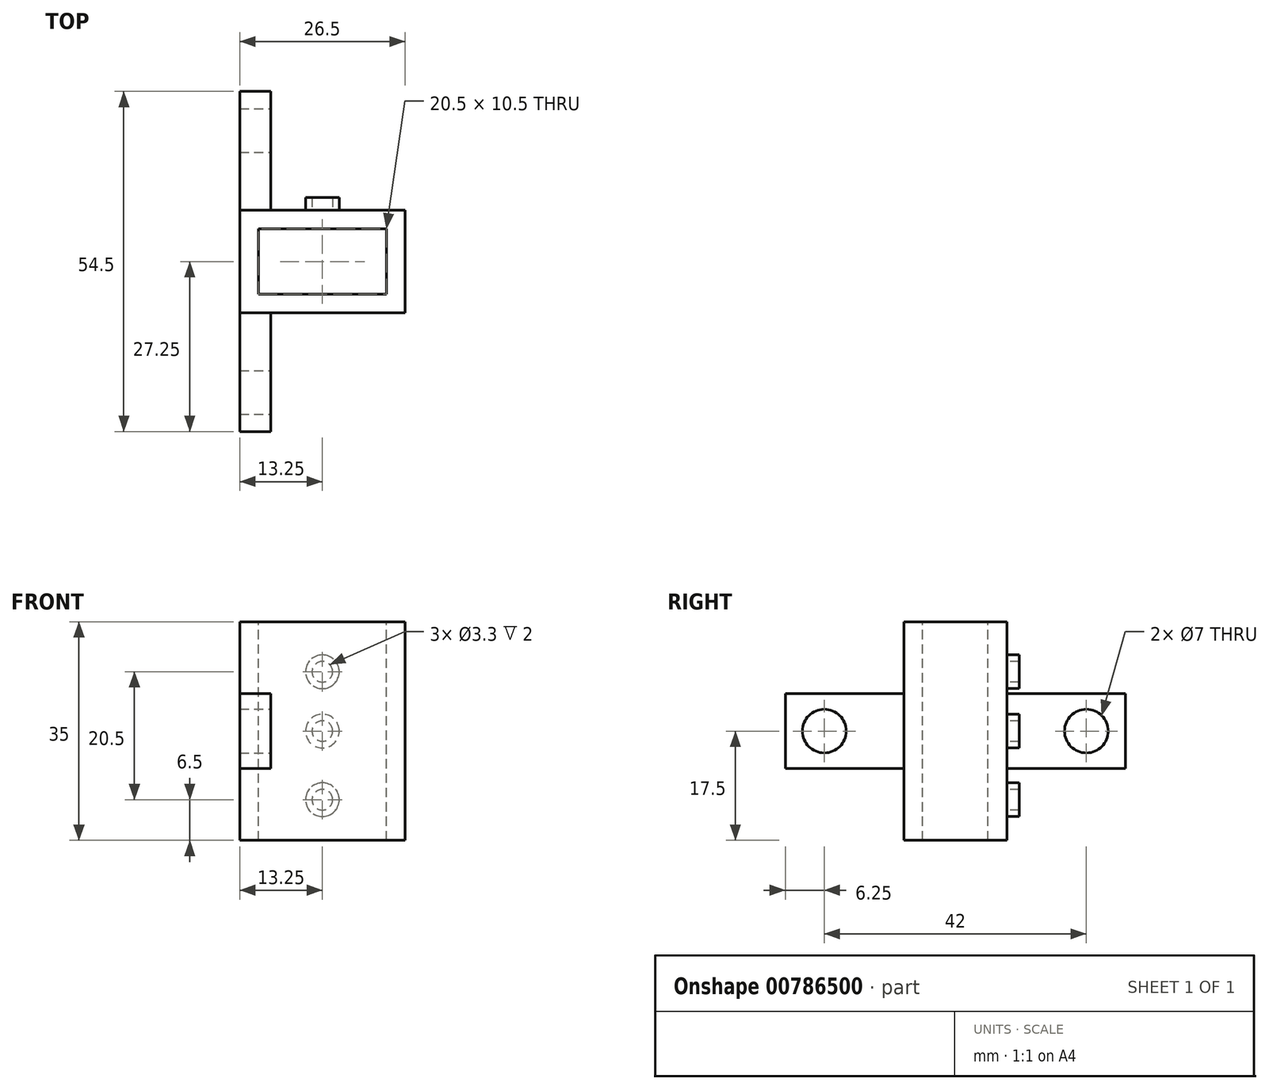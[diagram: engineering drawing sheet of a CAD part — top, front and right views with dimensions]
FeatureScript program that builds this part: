
annotation { "Feature Type Name" : "Feature", "Feature Type Description" : "" }
export const myFeature = defineFeature(function(context is Context, id is Id, definition is map)
    precondition{}
    {
        {
            var Q0;
            Q0=qCreatedBy(makeId("Front.planeOp"),FACE);
            var sketch = newSketch(context, id + "F0", { "sketchPlane" : qUnion([Q0])});
            skLineSegment(sketch, "E0.bottom", {"start": v(-13.25, 17.5) * mm, "end": v(13.25, 17.5) * mm});
            skLineSegment(sketch, "E0.top", {"start": v(-13.25, -17.5) * mm, "end": v(13.25, -17.5) * mm});
            skLineSegment(sketch, "E0.left", {"start": v(-13.25, 17.5) * mm, "end": v(-13.25, -17.5) * mm});
            skLineSegment(sketch, "E0.right", {"start": v(13.25, 17.5) * mm, "end": v(13.25, -17.5) * mm});
            skSolve(sketch);
        }
        {
            var Q0;
            Q0=qSketchRegion(id+"F0",true);
            extrude(context, id + "F1", {"entities" : qUnion([Q0]), "depth" : 16.5 * mm, "offsetDistance" : 25 * mm});
        }
        {
            var Q0;
            Q0=makeQuery(id+"F1.opExtrude","SWEPT_FACE",FACE,{"disambiguationData":[OSD([sQuery(id+"F0.wireOp",EDGE,"E0.bottom")])]});
            var sketch = newSketch(context, id + "F2", { "sketchPlane" : qUnion([Q0])});
            skLineSegment(sketch, "E1.bottom", {"start": v(-10.25, -3) * mm, "end": v(10.25, -3) * mm});
            skLineSegment(sketch, "E1.top", {"start": v(-10.25, -13.5) * mm, "end": v(10.25, -13.5) * mm});
            skLineSegment(sketch, "E1.left", {"start": v(-10.25, -3) * mm, "end": v(-10.25, -13.5) * mm});
            skLineSegment(sketch, "E1.right", {"start": v(10.25, -3) * mm, "end": v(10.25, -13.5) * mm});
            skSolve(sketch);
        }
        {
            var Q0;
            Q0=qSketchRegion(id+"F2",true);
            extrude(context, id + "F3", {"entities" : qUnion([Q0]), "operationType" : NewBodyOperationType.REMOVE, "oppositeDirection" : true, "depth" : 35 * mm, "offsetDistance" : 25 * mm});
        }
        {
            var Q0;
            Q0=makeQuery(id+"F1.opExtrude","CAP_FACE",FACE,{"disambiguationData":[OSD([sQuery(id+"F0.wireOp",EDGE,"E0.bottom"),sQuery(id+"F0.wireOp",EDGE,"E0.top"),sQuery(id+"F0.wireOp",EDGE,"E0.left"),sQuery(id+"F0.wireOp",EDGE,"E0.right")])],"isStart":true});
            var sketch = newSketch(context, id + "F4", { "sketchPlane" : qUnion([Q0])});
            skCircle(sketch, "E2", {"center": v(0, 0) * mm, "radius": 1.65 * mm});
            skCircle(sketch, "E3", {"center": v(0, 0) * mm, "radius": 2.7 * mm});
            skCircle(sketch, "E4.MirrorC", {"center": v(0, 9.5) * mm, "radius": 1.65 * mm});
            skCircle(sketch, "E5.MirrorC", {"center": v(0, 9.5) * mm, "radius": 2.7 * mm});
            skCircle(sketch, "E6.MirrorC", {"center": v(0, -11) * mm, "radius": 1.65 * mm});
            skCircle(sketch, "E7.MirrorC", {"center": v(0, -11) * mm, "radius": 2.7 * mm});
            skSolve(sketch);
        }
        {
            var Q0;
            Q0=qSketchRegion(id+"F4",true);
            extrude(context, id + "F5", {"entities" : qUnion([Q0]), "operationType" : NewBodyOperationType.ADD, "depth" : 2 * mm, "offsetDistance" : 25 * mm});
        }
        {
            var Q0;
            Q0=makeQuery(id+"F1.opExtrude","CAP_FACE",FACE,{"disambiguationData":[OSD([sQuery(id+"F0.wireOp",EDGE,"E0.bottom"),sQuery(id+"F0.wireOp",EDGE,"E0.top"),sQuery(id+"F0.wireOp",EDGE,"E0.left"),sQuery(id+"F0.wireOp",EDGE,"E0.right")])],"isStart":false});
            var sketch = newSketch(context, id + "F6", { "sketchPlane" : qUnion([Q0])});
            skLineSegment(sketch, "E8.bottom", {"start": v(-13.25, 6) * mm, "end": v(-8.25, 6) * mm});
            skLineSegment(sketch, "E8.top", {"start": v(-13.25, -6) * mm, "end": v(-8.25, -6) * mm});
            skLineSegment(sketch, "E8.left", {"start": v(-13.25, 6) * mm, "end": v(-13.25, -6) * mm});
            skLineSegment(sketch, "E8.right", {"start": v(-8.25, 6) * mm, "end": v(-8.25, -6) * mm});
            skSolve(sketch);
        }
        {
            var Q0;
            Q0=qSketchRegion(id+"F6",true);
            extrude(context, id + "F7", {"entities" : qUnion([Q0]), "operationType" : NewBodyOperationType.ADD, "depth" : 19 * mm, "offsetDistance" : 25 * mm});
        }
        {
            var Q0;
            {var subQ0=sQuery(id+"F0.wireOp",EDGE,"E0.left");var subQ1=sQuery(id+"F0.wireOp",EDGE,"E0.top");var subQ2=sQuery(id+"F0.wireOp",EDGE,"E0.right");var subQ3=sQuery(id+"F0.wireOp",EDGE,"E0.bottom");Q0=makeQuery(id+"F5.boolean.opBoolean","SPLIT",FACE,{"disambiguationData":[TD([makeQuery(id+"F1.opExtrude","SWEPT_FACE",FACE,{"disambiguationData":[OSD([subQ3])]})])],"derivedFrom":makeQuery(id+"F1.opExtrude","CAP_FACE",FACE,{"disambiguationData":[OSD([subQ3,subQ1,subQ0,subQ2])],"isStart":true})});}
            var sketch = newSketch(context, id + "F8", { "sketchPlane" : qUnion([Q0])});
            skLineSegment(sketch, "E9.bottom", {"start": v(13.25, 6) * mm, "end": v(8.25, 6) * mm});
            skLineSegment(sketch, "E9.top", {"start": v(13.25, -6) * mm, "end": v(8.25, -6) * mm});
            skLineSegment(sketch, "E9.left", {"start": v(13.25, 6) * mm, "end": v(13.25, -6) * mm});
            skLineSegment(sketch, "E9.right", {"start": v(8.25, 6) * mm, "end": v(8.25, -6) * mm});
            skSolve(sketch);
        }
        {
            var Q0;
            Q0=qSketchRegion(id+"F8",true);
            extrude(context, id + "F9", {"entities" : qUnion([Q0]), "operationType" : NewBodyOperationType.ADD, "depth" : 19 * mm, "offsetDistance" : 25 * mm});
        }
        {
            var Q0;
            Q0=makeQuery(id+"F9.opExtrude","SWEPT_FACE",FACE,{"disambiguationData":[OSD([sQuery(id+"F8.wireOp",EDGE,"E9.right")])]});
            var sketch = newSketch(context, id + "F10", { "sketchPlane" : qUnion([Q0])});
            skCircle(sketch, "E10", {"center": v(12.75, 0) * mm, "radius": 3.5 * mm});
            skPoint(sketch, "E10.centerSnap0", {"position": v(9.5, -6) * mm});
            skSolve(sketch);
        }
        {
            var Q0;
            Q0=qSketchRegion(id+"F10",true);
            extrude(context, id + "F11", {"entities" : qUnion([Q0]), "operationType" : NewBodyOperationType.REMOVE, "oppositeDirection" : true, "depth" : 5 * mm, "offsetDistance" : 25 * mm});
        }
        {
            var Q0;
            Q0=makeQuery(id+"F7.opExtrude","SWEPT_FACE",FACE,{"disambiguationData":[OSD([sQuery(id+"F6.wireOp",EDGE,"E8.right")])]});
            var sketch = newSketch(context, id + "F12", { "sketchPlane" : qUnion([Q0])});
            skCircle(sketch, "E11", {"center": v(-29.25, 0) * mm, "radius": 3.5 * mm});
            skPoint(sketch, "E11.centerSnap0", {"position": v(-26, 6) * mm});
            skSolve(sketch);
        }
        {
            var Q0;
            Q0=qSketchRegion(id+"F12",true);
            extrude(context, id + "F13", {"entities" : qUnion([Q0]), "operationType" : NewBodyOperationType.REMOVE, "oppositeDirection" : true, "depth" : 5 * mm, "offsetDistance" : 25 * mm});
        }
    });
